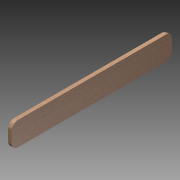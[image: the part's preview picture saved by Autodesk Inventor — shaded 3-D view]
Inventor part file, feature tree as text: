
AUTODESK INVENTOR PART (.ipt)
format: ipt  version: 2014 SP1 (Build 180222100, 222)  size: 99,840 bytes
history: native  units: in
note: dims shown in document units (in); Inventor stores cm internally (conversion verified against a paired STEP export)
features: extrude x1, fillet x1, sketch x1
ambient origin geometry x8: Origin, YZ Plane, XZ Plane, XY Plane, X Axis, Y Axis, Z Axis, Center Point
bodies: Solid1 (feature_tree)
feature tree (3):
  extrude  "Extrusion1"  Depth=0.75in
  fillet  "Fillet1"  Radius=33.625in
  sketch  "Sketch1"  dims[d0=5.0in d1=0.75in d2=33.625in d3=0.0in d4=1.3125in]
